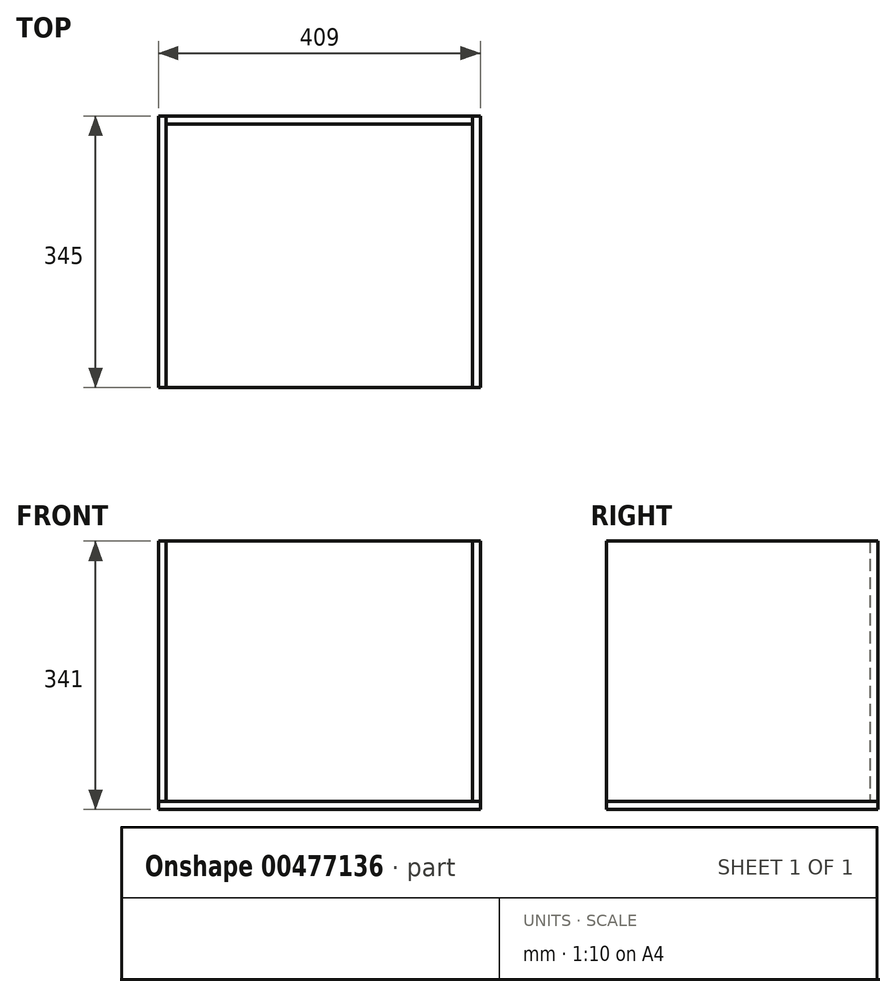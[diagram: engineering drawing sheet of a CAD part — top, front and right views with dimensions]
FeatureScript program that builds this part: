
annotation { "Feature Type Name" : "Feature", "Feature Type Description" : "" }
export const myFeature = defineFeature(function(context is Context, id is Id, definition is map)
    precondition{}
    {
        {
            var Q0;
            Q0=qCreatedBy(makeId("Top.planeOp"),FACE);
            var sketch = newSketch(context, id + "F0", { "sketchPlane" : qUnion([Q0])});
            skLineSegment(sketch, "E0.bottom", {"start": v(204.5, -172.5) * mm, "end": v(-204.5, -172.5) * mm});
            skLineSegment(sketch, "E0.top", {"start": v(204.5, 172.5) * mm, "end": v(-204.5, 172.5) * mm});
            skLineSegment(sketch, "E0.left", {"start": v(204.5, -172.5) * mm, "end": v(204.5, 172.5) * mm});
            skLineSegment(sketch, "E0.right", {"start": v(-204.5, -172.5) * mm, "end": v(-204.5, 172.5) * mm});
            skPoint(sketch, "E0.middle", {"position": v(0, 0) * mm});
            skSolve(sketch);
        }
        {
            var Q0;
            Q0 = qSketchRegion(id + "F0", true);
            extrude(context, id + "F1", {"entities" : qUnion([Q0]), "depth" : 10 * mm});
        }
        {
            var Q0;
            Q0=makeQuery(id+"F1.opExtrude","CAP_FACE",FACE,{"disambiguationData":[OSD([sQuery(id+"F0.wireOp",EDGE,"E0.bottom"),sQuery(id+"F0.wireOp",EDGE,"E0.top"),sQuery(id+"F0.wireOp",EDGE,"E0.left"),sQuery(id+"F0.wireOp",EDGE,"E0.right")])],"isStart":false});
            var sketch = newSketch(context, id + "F2", { "sketchPlane" : qUnion([Q0])});
            skLineSegment(sketch, "E1.bottom", {"start": v(-204.5, 172.5) * mm, "end": v(-194.5, 172.5) * mm});
            skLineSegment(sketch, "E1.top", {"start": v(-204.5, -172.5) * mm, "end": v(-194.5, -172.5) * mm});
            skLineSegment(sketch, "E1.left", {"start": v(-204.5, 172.5) * mm, "end": v(-204.5, -172.5) * mm});
            skLineSegment(sketch, "E1.right", {"start": v(-194.5, 172.5) * mm, "end": v(-194.5, -172.5) * mm});
            skLineSegment(sketch, "E2.bottom", {"start": v(204.5, 172.5) * mm, "end": v(194.5, 172.5) * mm});
            skLineSegment(sketch, "E2.top", {"start": v(204.5, -172.5) * mm, "end": v(194.5, -172.5) * mm});
            skLineSegment(sketch, "E2.left", {"start": v(204.5, 172.5) * mm, "end": v(204.5, -172.5) * mm});
            skLineSegment(sketch, "E2.right", {"start": v(194.5, 172.5) * mm, "end": v(194.5, -172.5) * mm});
            skLineSegment(sketch, "E3.bottom", {"start": v(-194.5, 172.5) * mm, "end": v(194.5, 172.5) * mm});
            skLineSegment(sketch, "E3.top", {"start": v(-194.5, 162.5) * mm, "end": v(194.5, 162.5) * mm});
            skLineSegment(sketch, "E3.left", {"start": v(-194.5, 172.5) * mm, "end": v(-194.5, 162.5) * mm});
            skLineSegment(sketch, "E3.right", {"start": v(194.5, 172.5) * mm, "end": v(194.5, 162.5) * mm});
            skSolve(sketch);
        }
        {
            assignVariable(context, id + "F3", {"name" : "H", "anyValue" : 331});
        }
        {
            var Q0;
            Q0=makeQuery(id+"F2.imprint","IMPRINT",FACE,{"disambiguationData":[TD([[makeQuery(id+"F2.imprint","IMPRINT",EDGE,{"derivedFrom":sQuery(id+"F2.wireOp",EDGE,"E3.bottom")}),1.0]])]});
            extrude(context, id + "F4", {"entities" : qUnion([Q0]), "depth" : (getVariable(context, 'H')) * mm});
        }
        {
            var Q0;
            Q0=makeQuery(id+"F2.imprint","IMPRINT",FACE,{"disambiguationData":[TD([[makeQuery(id+"F2.imprint","IMPRINT",EDGE,{"derivedFrom":sQuery(id+"F2.wireOp",EDGE,"E1.bottom")}),1.0]])]});
            extrude(context, id + "F5", {"entities" : qUnion([Q0]), "depth" : (getVariable(context, 'H')) * mm});
        }
        {
            var Q0;
            Q0=makeQuery(id+"F2.imprint","IMPRINT",FACE,{"disambiguationData":[TD([[makeQuery(id+"F2.imprint","IMPRINT",EDGE,{"derivedFrom":sQuery(id+"F2.wireOp",EDGE,"E2.bottom")}),1.0]])]});
            extrude(context, id + "F6", {"entities" : qUnion([Q0]), "depth" : (getVariable(context, 'H')) * mm});
        }
    });
